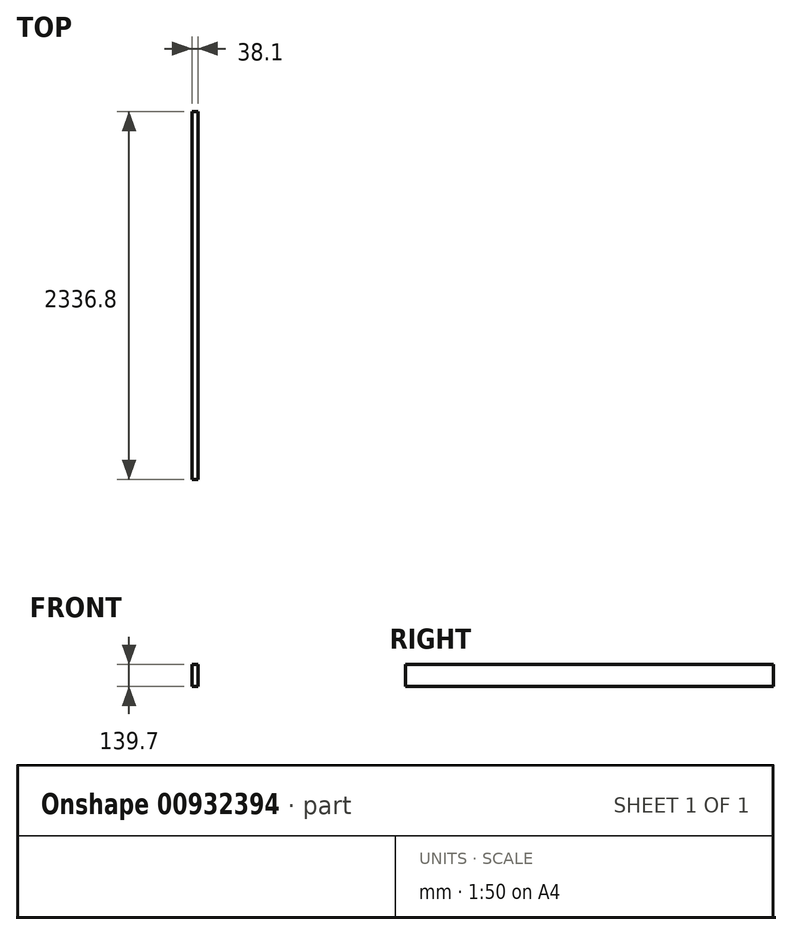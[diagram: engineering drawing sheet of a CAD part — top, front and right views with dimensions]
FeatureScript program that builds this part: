
annotation { "Feature Type Name" : "Feature", "Feature Type Description" : "" }
export const myFeature = defineFeature(function(context is Context, id is Id, definition is map)
    precondition{}
    {
        {
            var Q0;
            Q0=qCreatedBy(makeId("Front.planeOp"),FACE);
            var sketch = newSketch(context, id + "F0", { "sketchPlane" : qUnion([Q0])});
            skLineSegment(sketch, "E0.bottom", {"start": v(-19.05, 69.85) * mm, "end": v(19.05, 69.85) * mm});
            skLineSegment(sketch, "E0.top", {"start": v(-19.05, -69.85) * mm, "end": v(19.05, -69.85) * mm});
            skLineSegment(sketch, "E0.left", {"start": v(-19.05, 69.85) * mm, "end": v(-19.05, -69.85) * mm});
            skLineSegment(sketch, "E0.right", {"start": v(19.05, 69.85) * mm, "end": v(19.05, -69.85) * mm});
            skPoint(sketch, "E0.middle", {"position": v(0, 0) * mm});
            skSolve(sketch);
        }
        {
            var Q0;
            Q0=makeQuery(id+"F0.imprint","IMPRINT",FACE,{"disambiguationData":[TD([[makeQuery(id+"F0.imprint","IMPRINT",EDGE,{"derivedFrom":sQuery(id+"F0.wireOp",EDGE,"E0.bottom")}),-1.0]])]});
            extrude(context, id + "F1", {"entities" : qUnion([Q0]), "depth" : 2336.8 * mm, "offsetDistance" : 25.4 * mm});
        }
    });
